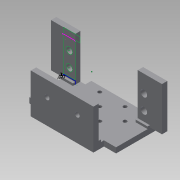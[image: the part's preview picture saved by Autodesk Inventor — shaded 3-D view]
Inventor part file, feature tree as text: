
AUTODESK INVENTOR PART (.ipt)
format: ipt  version: 2015 SP1 (Build 190203100, 203)  size: 387,072 bytes
history: native  units: in
note: dims shown in document units (in); Inventor stores cm internally (conversion verified against a paired STEP export)
features: sketch x19, extrude x15, mirror x7, projected_geometry x4, fillet x2, reference x2, other x1, imported_body x1
ambient origin geometry x8: Origin, YZ Plane, XZ Plane, XY Plane, X Axis, Y Axis, Z Axis, Center Point
bodies: Body1 (feature_tree)
feature tree (51):
  fillet  "Fillet5"  Radius=0.782in
  other  "asb-041"
  sketch  "Sketch1"  dims[d1=2.25in d2=0.0779in d3=0.0in]
  extrude  "Extrusion1"  Depth=2.25in TaperAngle=0.0deg
  sketch  "Sketch8"  dims[d17=1.624in d18=0.0in d19=0.0779in d20=0.0in]
  extrude  "Extrusion4"  Depth=0.0778in
  sketch  "Sketch10"  dims[d22=0.313in d23=0.0in d27=0.313in d28=0.0in]
  extrude  "Extrusion5"  Depth=1.624in TaperAngle=0.0deg
  extrude  "Extrusion6"  Depth=0.313in TaperAngle=0.0deg
  sketch  "Sketch14"  dims[d35=0.1378in d36=0.0in d37=0.313in]
  extrude  "Extrusion7"  Depth=0.01in
  mirror  "Mirror2"
  sketch  "Sketch17"  dims[d38=0.1378in d39=0.0in d40=0.0773in d41=0.0591in]
  extrude  "Extrusion8"  Depth=0.313in
  extrude  "Extrusion9"  Depth=0.0591in
  mirror  "Mirror3"
  fillet  "Fillet1"  Radius=0.0591in
  mirror  "Mirror4"
  extrude  "Extrusion10"  Depth=1.624in TaperAngle=0.0deg
  extrude  "Extrusion11"  Depth=0.0591in
  mirror  "Mirror5"
  sketch  "Sketch25"  dims[d53=1.624in d54=0.0in d55=0.313in d56=0.0in]
  sketch  "Sketch26"  dims[d57=0.1378in d58=0.0in]
  sketch  "Sketch27"
  extrude  "Extrusion12"  Depth=0.1378in TaperAngle=0.0deg
  sketch  "Sketch28"
  sketch  "Sketch29"
  extrude  "Extrusion13"  Depth=0.313in TaperAngle=0.0deg
  mirror  "Mirror6"
  extrude  "Extrusion14"  [1 undecoded]
  extrude  "Extrusion15"  [1 undecoded]
  extrude  "Extrusion16"  [1 undecoded]
  mirror  "Mirror7"
  extrude  "Extrusion17"  [1 undecoded]
  mirror  "Mirror8"
  imported_body  "Base1"
  sketch  "Sketch2"  dims[d14=0.0779in d15=0.0in d16=0.0778in]
  projected_geometry  "Projected Loop1"
  projected_geometry  "Projected Loop6"
  sketch  "Sketch13"  dims[d29=0.313in d30=0.0in d32=0.01in]
  projected_geometry  "Projected Loop7"
  projected_geometry  "Projected Loop8"
  sketch  "Sketch19"  dims[d42=0.0591in d43=1.624in d44=0.0in]
  sketch  "Sketch23"  dims[d46=0.0591in d47=0.0591in]
  reference  "Reference1"
  sketch  "Sketch24"  dims[d48=0.313in d49=0.0in d51=0.1378in d52=0.0in]
  reference  "Reference2"
  sketch  "Sketch30"
  sketch  "Sketch31"
  sketch  "Sketch32"
  sketch  "Sketch33"
note: 4 required parameter values undecoded (feature->parameter linkage not recoverable at this tier; creation-order binding heuristic only, values carry confidence <= 0.55)
